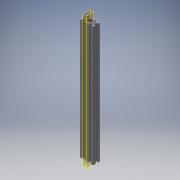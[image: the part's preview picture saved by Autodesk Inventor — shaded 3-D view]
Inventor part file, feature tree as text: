
AUTODESK INVENTOR PART (.ipt)
format: ipt  version: 2018 (Build 220112000, 112)  size: 350,208 bytes
history: native  units: mm
features: plane x2, extrude x1, sketch x1, projected_geometry x1, imported_body x1
ambient origin geometry x8: Origin, YZ Plane, XZ Plane, XY Plane, X Axis, Y Axis, Z Axis, Center Point
bodies: Solid1 (feature_tree)
feature tree (6):
  extrude  "Extrusion1"  [1 undecoded]
  plane  "Work Plane3"
  sketch  "Sketch1"  dims[d0=650.0mm d1=0.0mm d2=-10.0mm]
  projected_geometry  "Projected Loop1"
  plane  "Work Plane2"
  imported_body  "Base1"
note: 1 required parameter value undecoded (feature->parameter linkage not recoverable at this tier; creation-order binding heuristic only, values carry confidence <= 0.55)
